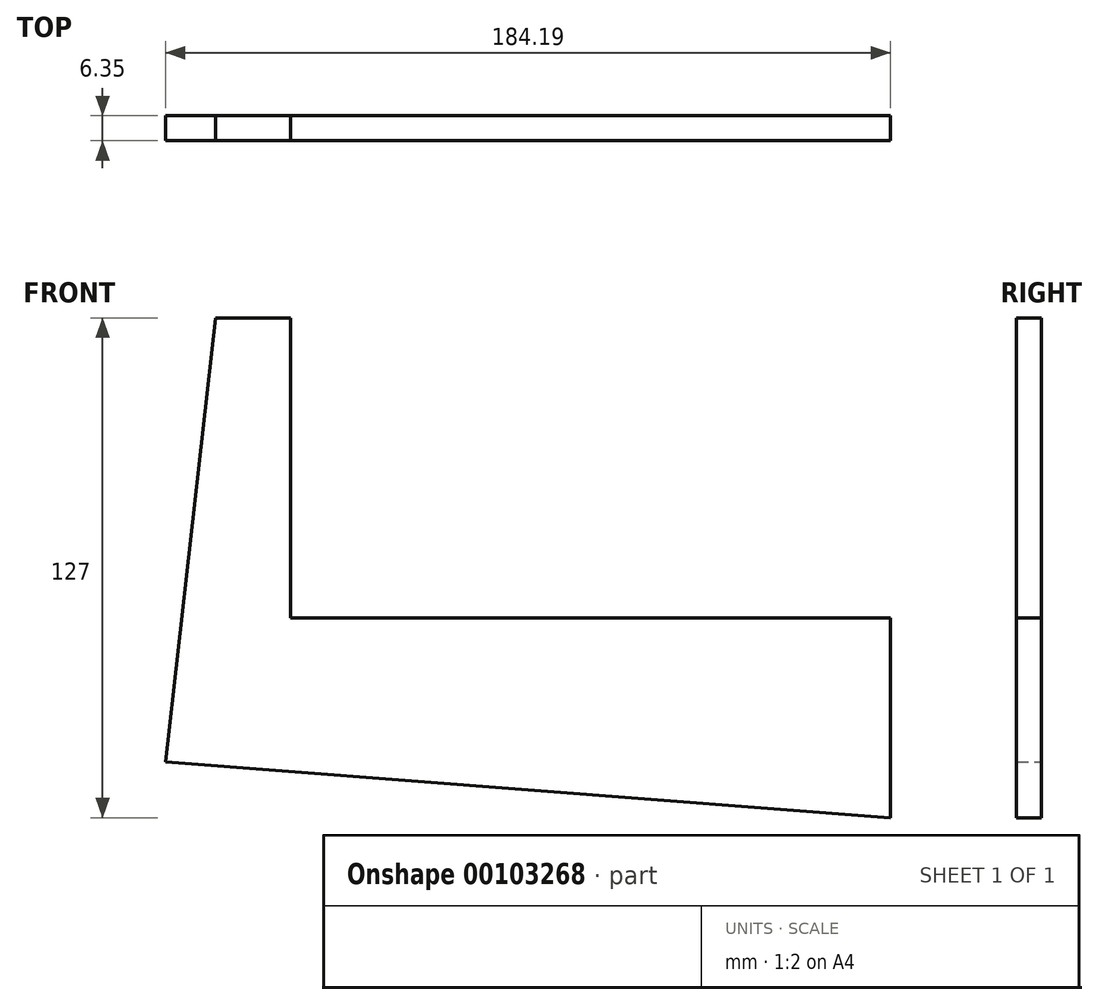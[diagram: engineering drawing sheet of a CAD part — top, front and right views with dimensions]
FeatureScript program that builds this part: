
annotation { "Feature Type Name" : "Feature", "Feature Type Description" : "" }
export const myFeature = defineFeature(function(context is Context, id is Id, definition is map)
    precondition{}
    {
        {
            var Q0;
            Q0=qCreatedBy(makeId("Front.planeOp"),FACE);
            var sketch = newSketch(context, id + "F0", { "sketchPlane" : qUnion([Q0])});
            skLineSegment(sketch, "E0", {"start": v(0, 0) * mm, "end": v(0, 50.8) * mm});
            skLineSegment(sketch, "E1", {"start": v(0, 50.8) * mm, "end": v(-152.4, 50.8) * mm});
            skLineSegment(sketch, "E2", {"start": v(-152.4, 50.8) * mm, "end": v(-152.4, 127) * mm});
            skLineSegment(sketch, "E3", {"start": v(-152.4, 127) * mm, "end": v(-171.45, 127) * mm});
            skLineSegment(sketch, "E4", {"start": v(-171.45, 127) * mm, "end": v(-184.19, 14.22) * mm});
            skLineSegment(sketch, "E5", {"start": v(-184.19, 14.22) * mm, "end": v(0, 0) * mm});
            skSolve(sketch);
        }
        {
            var Q0;
            Q0=makeQuery(id+"F0.imprint","IMPRINT",FACE,{"disambiguationData":[TD([[makeQuery(id+"F0.imprint","IMPRINT",EDGE,{"derivedFrom":sQuery(id+"F0.wireOp",EDGE,"E0")}),1.0]])]});
            extrude(context, id + "F1", {"entities" : qUnion([Q0]), "depth" : 6.35 * mm});
        }
    });
